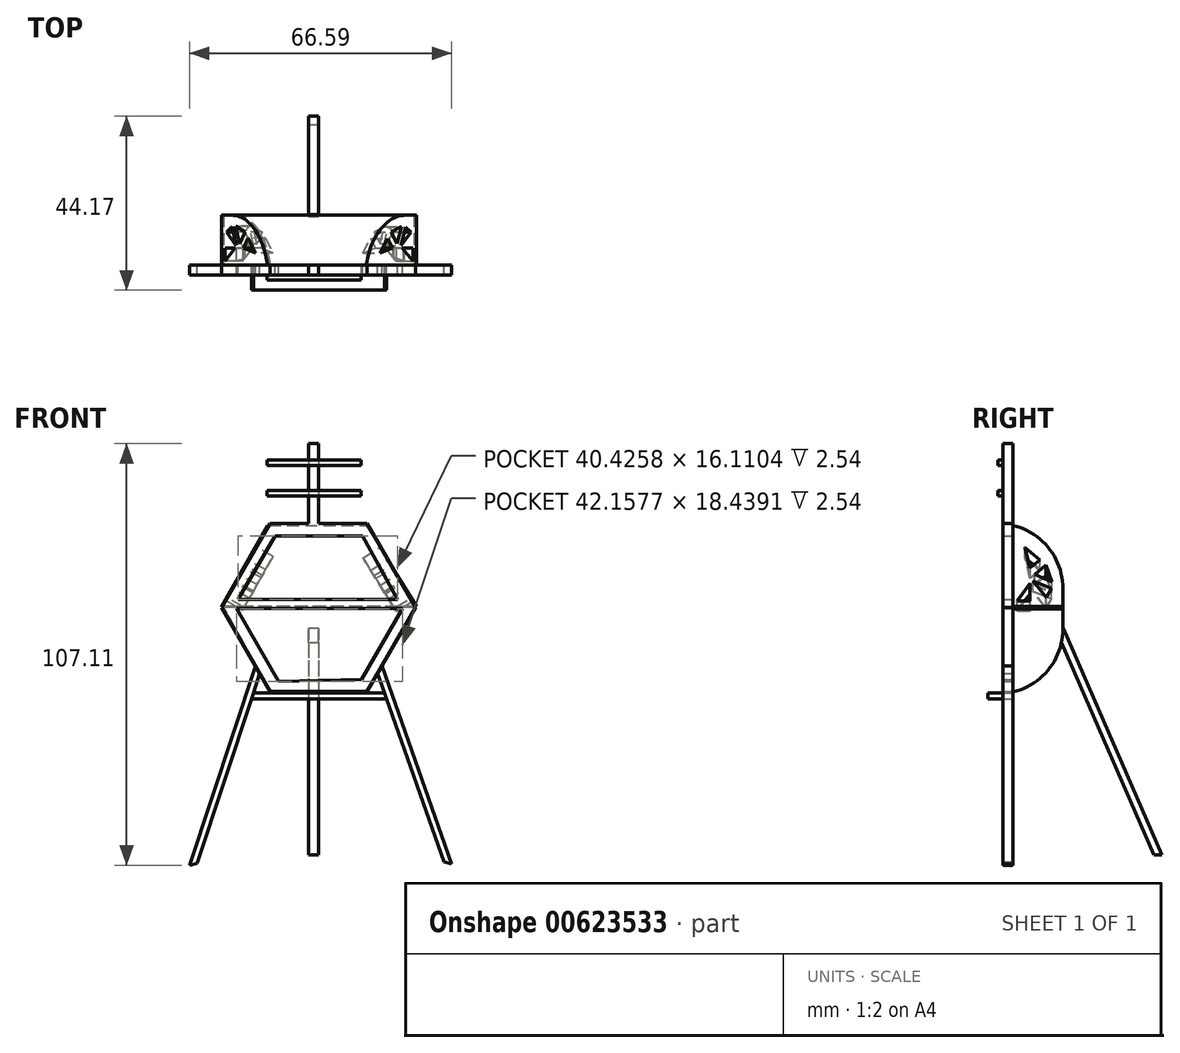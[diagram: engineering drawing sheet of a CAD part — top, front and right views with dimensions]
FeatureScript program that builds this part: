
annotation { "Feature Type Name" : "Feature", "Feature Type Description" : "" }
export const myFeature = defineFeature(function(context is Context, id is Id, definition is map)
    precondition{}
    {
        {
            var Q0;
            Q0=qCreatedBy(makeId("Front.planeOp"),FACE);
            var sketch = newSketch(context, id + "F0", { "sketchPlane" : qUnion([Q0])});
            skCircle(sketch, "E0.cCircle", {"center": v(0, 45.92) * mm, "radius": 21.32 * mm, "construction": true});
            skLineSegment(sketch, "E0.0", {"start": v(12.3, 24.6) * mm, "end": v(-12.3, 24.6) * mm});
            skLineSegment(sketch, "E0.1", {"start": v(-12.3, 24.6) * mm, "end": v(-24.62, 45.92) * mm});
            skLineSegment(sketch, "E0.2", {"start": v(-24.62, 45.92) * mm, "end": v(-12.3, 67.24) * mm});
            skLineSegment(sketch, "E0.3", {"start": v(-12.3, 67.24) * mm, "end": v(12.3, 67.24) * mm});
            skLineSegment(sketch, "E0.4", {"start": v(12.3, 67.24) * mm, "end": v(24.62, 45.92) * mm});
            skLineSegment(sketch, "E0.5", {"start": v(24.62, 45.92) * mm, "end": v(12.3, 24.6) * mm});
            skPoint(sketch, "E0.0.midPoint", {"position": v(0, 24.6) * mm});
            skLineSegment(sketch, "E1", {"start": v(-16.63, 24.26) * mm, "end": v(16.72, 24.26) * mm});
            skLineSegment(sketch, "E2", {"start": v(17.24, 22.76) * mm, "end": v(-17.18, 22.76) * mm});
            skLineSegment(sketch, "E3", {"start": v(-11.12, 64.11) * mm, "end": v(-21.31, 46.45) * mm});
            skLineSegment(sketch, "E4", {"start": v(-21.31, 46.45) * mm, "end": v(-10.18, 27.19) * mm});
            skLineSegment(sketch, "E5", {"start": v(-10.18, 27.19) * mm, "end": v(10.91, 27.6) * mm});
            skLineSegment(sketch, "E6", {"start": v(10.91, 27.6) * mm, "end": v(21.32, 45.62) * mm});
            skLineSegment(sketch, "E7", {"start": v(21.32, 45.62) * mm, "end": v(11.12, 64.11) * mm});
            skLineSegment(sketch, "E8", {"start": v(11.12, 64.11) * mm, "end": v(-11.12, 64.11) * mm});
            skLineSegment(sketch, "E9", {"start": v(-20.42, 48) * mm, "end": v(20, 48) * mm});
            skLineSegment(sketch, "E10", {"start": v(20, 48) * mm, "end": v(21.32, 45.62) * mm});
            skLineSegment(sketch, "E11", {"start": v(21.32, 45.62) * mm, "end": v(-20.84, 45.62) * mm});
            skLineSegment(sketch, "E12", {"start": v(-14.96, 29.2) * mm, "end": v(-30.9, -19.05) * mm});
            skLineSegment(sketch, "E13", {"start": v(14.96, 29.2) * mm, "end": v(31.85, -18.72) * mm});
            skLineSegment(sketch, "E14", {"start": v(-16.06, 31.1) * mm, "end": v(-32.8, -19.55) * mm});
            skLineSegment(sketch, "E15", {"start": v(-32.8, -19.55) * mm, "end": v(-30.9, -19.05) * mm});
            skLineSegment(sketch, "E16", {"start": v(16.07, 31.1) * mm, "end": v(33.8, -19.2) * mm});
            skLineSegment(sketch, "E17", {"start": v(33.8, -19.2) * mm, "end": v(31.85, -18.72) * mm});
            skSolve(sketch);
        }
        {
            var Q0;
            {var subQ4=sQuery(id+"F0.wireOp",EDGE,"E0.0");Q0=makeQuery(id+"F0.imprint","IMPRINT",FACE,{"disambiguationData":[TD([[makeQuery(id+"F0.imprint","IMPRINT",EDGE,{"derivedFrom":subQ4}),-1.0]])]});}
            var Q1;
            {var subQ0=sQuery(id+"F0.wireOp",EDGE,"xqdiFxsL-KJle-jqia-ZrNX-kboYkiIlxZ25");Q1=makeQuery(id+"F0.imprint","IMPRINT",FACE,{"disambiguationData":[TD([[makeQuery(id+"F0.imprint","IMPRINT",EDGE,{"derivedFrom":subQ0}),1.0]])]});}
            var Q2;
            {var subQ0=sQuery(id+"F0.wireOp",EDGE,"LFHcvuUA-xukv-JVWA-ilLV-98vBFIWMlgdJ");Q2=makeQuery(id+"F0.imprint","IMPRINT",FACE,{"disambiguationData":[TD([[makeQuery(id+"F0.imprint","IMPRINT",EDGE,{"derivedFrom":subQ0}),-1.0]])]});}
            extrude(context, id + "F1", {"entities" : qUnion([Q0, Q1, Q2]), "depth" : 2.54 * mm, "offsetDistance" : 25.4 * mm});
        }
        {
            var Q0;
            {var subQ0=sQuery(id+"F0.wireOp",EDGE,"E1");Q0=makeQuery(id+"F0.imprint","IMPRINT",FACE,{"disambiguationData":[TD([[makeQuery(id+"F0.imprint","IMPRINT",EDGE,{"derivedFrom":subQ0}),-1.0]])]});}
            extrude(context, id + "F2", {"entities" : qUnion([Q0]), "operationType" : NewBodyOperationType.ADD, "depth" : 6.35 * mm, "offsetDistance" : 25.4 * mm});
        }
        {
            var Q0;
            {var subQ0=sQuery(id+"F0.wireOp",EDGE,"E9");Q0=makeQuery(id+"F0.imprint","IMPRINT",FACE,{"disambiguationData":[TD([[makeQuery(id+"F0.imprint","IMPRINT",EDGE,{"derivedFrom":subQ0}),-1.0]])]});}
            extrude(context, id + "F3", {"entities" : qUnion([Q0]), "operationType" : NewBodyOperationType.ADD, "depth" : 2.54 * mm, "offsetDistance" : 25.4 * mm});
        }
        {
            var Q0;
            Q0=qCreatedBy(makeId("Front.planeOp"),FACE);
            var sketch = newSketch(context, id + "F4", { "sketchPlane" : qUnion([Q0])});
            skLineSegment(sketch, "E18", {"start": v(24.9, 46.2) * mm, "end": v(-24.6, 46.2) * mm});
            skLineSegment(sketch, "E19", {"start": v(-24.6, 46.2) * mm, "end": v(-13, 66.8) * mm});
            skLineSegment(sketch, "E20", {"start": v(-13, 66.8) * mm, "end": v(12.08, 66.8) * mm});
            skLineSegment(sketch, "E21", {"start": v(12.08, 66.8) * mm, "end": v(24.9, 46.2) * mm});
            skSolve(sketch);
        }
        {
            var Q0;
            Q0 = qSketchRegion(id + "F4", true);
            extrude(context, id + "F5", {"entities" : qUnion([Q0]), "operationType" : NewBodyOperationType.ADD, "oppositeDirection" : true, "depth" : 12.7 * mm, "offsetDistance" : 25.4 * mm});
        }
        {
            var Q0;
            Q0=makeQuery(id+"F5.opExtrude","CAP_EDGE",EDGE,{"disambiguationData":[OSD([sQuery(id+"F4.wireOp",EDGE,"E20")])],"isStart":false});
            fillet(context, id + "F6", {"entities" : qUnion([Q0]), "radius" : 16.5 * mm, "tangentPropagation" : true, "allowEdgeOverflow" : false});
        }
        {
            var Q0;
            {var subQ1=sQuery(id+"F0.wireOp",EDGE,"E0.0");Q0=makeQuery(id+"F0.imprint","IMPRINT",FACE,{"disambiguationData":[TD([[makeQuery(id+"F0.imprint","IMPRINT",EDGE,{"derivedFrom":subQ1}),-1.0]])]});}
            var sketch = newSketch(context, id + "F7", { "sketchPlane" : qUnion([Q0])});
            skLineSegment(sketch, "E22", {"start": v(-24.16, 46.1) * mm, "end": v(24.19, 46.1) * mm});
            skLineSegment(sketch, "E23", {"start": v(24.19, 46.1) * mm, "end": v(24.42, 45.61) * mm});
            skLineSegment(sketch, "E24", {"start": v(24.42, 45.61) * mm, "end": v(12.23, 24.43) * mm});
            skLineSegment(sketch, "E25", {"start": v(12.23, 24.43) * mm, "end": v(-12.24, 24.43) * mm});
            skLineSegment(sketch, "E26", {"start": v(-12.24, 24.43) * mm, "end": v(-24.16, 46.1) * mm});
            skSolve(sketch);
        }
        {
            var Q0;
            Q0 = qSketchRegion(id + "F7", true);
            extrude(context, id + "F8", {"entities" : qUnion([Q0]), "operationType" : NewBodyOperationType.ADD, "oppositeDirection" : true, "depth" : 12.7 * mm, "offsetDistance" : 25.4 * mm});
        }
        {
            var Q0;
            Q0=makeQuery(id+"F8.opExtrude","CAP_EDGE",EDGE,{"disambiguationData":[OSD([sQuery(id+"F7.wireOp",EDGE,"E25")])],"isStart":false});
            fillet(context, id + "F9", {"entities" : qUnion([Q0]), "radius" : 16.5 * mm, "tangentPropagation" : true, "allowEdgeOverflow" : false});
        }
        {
            var Q0;
            Q0=makeQuery(id+"F5.opExtrude","SWEPT_FACE",FACE,{"disambiguationData":[OSD([sQuery(id+"F4.wireOp",EDGE,"E21")])]});
            var sketch = newSketch(context, id + "F10", { "sketchPlane" : qUnion([Q0])});
            skLineSegment(sketch, "E27", {"start": v(3.02, 43.8) * mm, "end": v(6.81, 40.05) * mm});
            skLineSegment(sketch, "E28", {"start": v(6.81, 40.05) * mm, "end": v(4.35, 37.56) * mm});
            skLineSegment(sketch, "E29", {"start": v(4.35, 37.56) * mm, "end": v(3.02, 43.8) * mm});
            skLineSegment(sketch, "E30", {"start": v(8.35, 38.44) * mm, "end": v(5.52, 35.58) * mm});
            skLineSegment(sketch, "E31", {"start": v(5.52, 35.58) * mm, "end": v(9.86, 33.34) * mm});
            skLineSegment(sketch, "E32", {"start": v(9.86, 33.34) * mm, "end": v(8.35, 38.44) * mm});
            skLineSegment(sketch, "E33", {"start": v(5.01, 33.65) * mm, "end": v(9.72, 31.5) * mm});
            skLineSegment(sketch, "E34", {"start": v(9.72, 31.5) * mm, "end": v(8.46, 28.73) * mm});
            skLineSegment(sketch, "E35", {"start": v(8.46, 28.73) * mm, "end": v(5.01, 33.65) * mm});
            skLineSegment(sketch, "E36", {"start": v(4.35, 33) * mm, "end": v(4.35, 27.8) * mm});
            skLineSegment(sketch, "E37", {"start": v(4.35, 27.8) * mm, "end": v(1.1, 27.8) * mm});
            skLineSegment(sketch, "E38", {"start": v(1.1, 27.8) * mm, "end": v(4.35, 33) * mm});
            skSolve(sketch);
        }
        {
            var Q0;
            Q0=makeQuery(id+"F5.opExtrude","SWEPT_FACE",FACE,{"disambiguationData":[OSD([sQuery(id+"F4.wireOp",EDGE,"E19")])]});
            var sketch = newSketch(context, id + "F11", { "sketchPlane" : qUnion([Q0])});
            skLineSegment(sketch, "E39", {"start": v(-3.04, 45.6) * mm, "end": v(-4.37, 39.43) * mm});
            skLineSegment(sketch, "E40", {"start": v(-4.37, 39.43) * mm, "end": v(-6.85, 41.79) * mm});
            skLineSegment(sketch, "E41", {"start": v(-6.85, 41.79) * mm, "end": v(-3.04, 45.6) * mm});
            skLineSegment(sketch, "E42", {"start": v(-8.37, 40.12) * mm, "end": v(-5.4, 37.41) * mm});
            skLineSegment(sketch, "E43", {"start": v(-5.4, 37.41) * mm, "end": v(-9.88, 35.26) * mm});
            skLineSegment(sketch, "E44", {"start": v(-9.88, 35.26) * mm, "end": v(-8.37, 40.12) * mm});
            skLineSegment(sketch, "E45", {"start": v(-9.76, 33.4) * mm, "end": v(-8.37, 30.75) * mm});
            skLineSegment(sketch, "E46", {"start": v(-8.37, 30.75) * mm, "end": v(-5.04, 35.54) * mm});
            skLineSegment(sketch, "E47", {"start": v(-5.04, 35.54) * mm, "end": v(-9.76, 33.4) * mm});
            skLineSegment(sketch, "E48", {"start": v(-4.31, 35.05) * mm, "end": v(-4.31, 29.93) * mm});
            skLineSegment(sketch, "E49", {"start": v(-4.31, 29.93) * mm, "end": v(-1, 29.93) * mm});
            skLineSegment(sketch, "E50", {"start": v(-1, 29.93) * mm, "end": v(-4.31, 35.05) * mm});
            skSolve(sketch);
        }
        {
            var Q0;
            {var subQ6=sQuery(id+"F0.wireOp",EDGE,"E14");Q0=makeQuery(id+"F0.imprint","IMPRINT",FACE,{"disambiguationData":[TD([[makeQuery(id+"F0.imprint","IMPRINT",EDGE,{"derivedFrom":subQ6}),1.0]])]});}
            var Q1;
            {var subQ6=sQuery(id+"F0.wireOp",EDGE,"E16");Q1=makeQuery(id+"F0.imprint","IMPRINT",FACE,{"disambiguationData":[TD([[makeQuery(id+"F0.imprint","IMPRINT",EDGE,{"derivedFrom":subQ6}),-1.0]])]});}
            extrude(context, id + "F12", {"entities" : qUnion([Q0, Q1]), "depth" : 2.54 * mm, "offsetDistance" : 25.4 * mm});
        }
        {
            var Q0;
            Q0=makeQuery(id+"F11.imprint","IMPRINT",FACE,{"disambiguationData":[TD([[makeQuery(id+"F11.imprint","IMPRINT",EDGE,{"derivedFrom":sQuery(id+"F11.wireOp",EDGE,"E39")}),-1.0]])]});
            var Q1;
            Q1=makeQuery(id+"F11.imprint","IMPRINT",FACE,{"disambiguationData":[TD([[makeQuery(id+"F11.imprint","IMPRINT",EDGE,{"derivedFrom":sQuery(id+"F11.wireOp",EDGE,"E42")}),-1.0]])]});
            var Q2;
            Q2=makeQuery(id+"F11.imprint","IMPRINT",FACE,{"disambiguationData":[TD([[makeQuery(id+"F11.imprint","IMPRINT",EDGE,{"derivedFrom":sQuery(id+"F11.wireOp",EDGE,"E45")}),1.0]])]});
            var Q3;
            Q3=makeQuery(id+"F11.imprint","IMPRINT",FACE,{"disambiguationData":[TD([[makeQuery(id+"F11.imprint","IMPRINT",EDGE,{"derivedFrom":sQuery(id+"F11.wireOp",EDGE,"E48")}),1.0]])]});
            var Q4;
            Q4=makeQuery(id+"F10.imprint","IMPRINT",FACE,{"disambiguationData":[TD([[makeQuery(id+"F10.imprint","IMPRINT",EDGE,{"derivedFrom":sQuery(id+"F10.wireOp",EDGE,"E27")}),-1.0]])]});
            var Q5;
            Q5=makeQuery(id+"F10.imprint","IMPRINT",FACE,{"disambiguationData":[TD([[makeQuery(id+"F10.imprint","IMPRINT",EDGE,{"derivedFrom":sQuery(id+"F10.wireOp",EDGE,"E36")}),-1.0]])]});
            var Q6;
            Q6=makeQuery(id+"F10.imprint","IMPRINT",FACE,{"disambiguationData":[TD([[makeQuery(id+"F10.imprint","IMPRINT",EDGE,{"derivedFrom":sQuery(id+"F10.wireOp",EDGE,"E33")}),-1.0]])]});
            var Q7;
            Q7=makeQuery(id+"F10.imprint","IMPRINT",FACE,{"disambiguationData":[TD([[makeQuery(id+"F10.imprint","IMPRINT",EDGE,{"derivedFrom":sQuery(id+"F10.wireOp",EDGE,"E30")}),1.0]])]});
            extrude(context, id + "F13", {"entities" : qUnion([Q0, Q1, Q2, Q3, Q4, Q5, Q6, Q7]), "operationType" : NewBodyOperationType.REMOVE, "oppositeDirection" : true, "depth" : 5.08 * mm, "offsetDistance" : 25.4 * mm});
        }
        {
            var Q0;
            Q0=makeQuery(id+"F10.imprint","IMPRINT",FACE,{"disambiguationData":[TD([[makeQuery(id+"F10.imprint","IMPRINT",EDGE,{"derivedFrom":sQuery(id+"F10.wireOp",EDGE,"E30")}),1.0]])]});
            var Q1;
            Q1=makeQuery(id+"F10.imprint","IMPRINT",FACE,{"disambiguationData":[TD([[makeQuery(id+"F10.imprint","IMPRINT",EDGE,{"derivedFrom":sQuery(id+"F10.wireOp",EDGE,"E33")}),-1.0]])]});
            var Q2;
            Q2=makeQuery(id+"F10.imprint","IMPRINT",FACE,{"disambiguationData":[TD([[makeQuery(id+"F10.imprint","IMPRINT",EDGE,{"derivedFrom":sQuery(id+"F10.wireOp",EDGE,"E36")}),-1.0]])]});
            var Q3;
            Q3=makeQuery(id+"F10.imprint","IMPRINT",FACE,{"disambiguationData":[TD([[makeQuery(id+"F10.imprint","IMPRINT",EDGE,{"derivedFrom":sQuery(id+"F10.wireOp",EDGE,"E27")}),-1.0]])]});
            extrude(context, id + "F14", {"entities" : qUnion([Q0, Q1, Q2, Q3]), "operationType" : NewBodyOperationType.REMOVE, "oppositeDirection" : true, "depth" : 5.08 * mm, "offsetDistance" : 25.4 * mm});
        }
        {
            var Q0;
            Q0=qCreatedBy(makeId("Right.planeOp"),FACE);
            var sketch = newSketch(context, id + "F15", { "sketchPlane" : qUnion([Q0])});
            skLineSegment(sketch, "E51", {"start": v(12.87, 40.67) * mm, "end": v(37.82, -16.89) * mm});
            skLineSegment(sketch, "E52", {"start": v(12.87, 40.67) * mm, "end": v(10.8, 40.67) * mm});
            skLineSegment(sketch, "E53", {"start": v(10.8, 40.67) * mm, "end": v(35.75, -16.89) * mm});
            skLineSegment(sketch, "E54", {"start": v(35.75, -16.89) * mm, "end": v(37.82, -16.89) * mm});
            skSolve(sketch);
        }
        {
            var Q0;
            Q0=makeQuery(id+"F15.imprint","IMPRINT",FACE,{"disambiguationData":[TD([[makeQuery(id+"F15.imprint","IMPRINT",EDGE,{"derivedFrom":sQuery(id+"F15.wireOp",EDGE,"E51")}),-1.0]])]});
            extrude(context, id + "F16", {"entities" : qUnion([Q0]), "operationType" : NewBodyOperationType.ADD, "oppositeDirection" : true, "depth" : 2.54 * mm, "offsetDistance" : 25.4 * mm});
        }
        {
            var Q0;
            Q0=makeQuery(id+"F1.opExtrude","SWEPT_FACE",FACE,{"disambiguationData":[OSD([sQuery(id+"F0.wireOp",EDGE,"E0.3")])]});
            var sketch = newSketch(context, id + "F17", { "sketchPlane" : qUnion([Q0])});
            skLineSegment(sketch, "E55.bottom", {"start": v(-2.55, 0) * mm, "end": v(0, 0) * mm});
            skLineSegment(sketch, "E55.top", {"start": v(-2.55, -2.54) * mm, "end": v(0, -2.54) * mm});
            skLineSegment(sketch, "E55.left", {"start": v(-2.55, 0) * mm, "end": v(-2.55, -2.54) * mm});
            skLineSegment(sketch, "E55.right", {"start": v(0, 0) * mm, "end": v(0, -2.54) * mm});
            skSolve(sketch);
        }
        {
            var Q0;
            Q0=makeQuery(id+"F17.imprint","IMPRINT",FACE,{"disambiguationData":[TD([[makeQuery(id+"F17.imprint","IMPRINT",EDGE,{"derivedFrom":sQuery(id+"F17.wireOp",EDGE,"E55.bottom")}),-1.0]])]});
            extrude(context, id + "F18", {"entities" : qUnion([Q0]), "operationType" : NewBodyOperationType.ADD, "depth" : 20.32 * mm, "offsetDistance" : 25.4 * mm});
        }
        {
            var Q0;
            {var subQ0=sQuery(id+"F0.wireOp",EDGE,"E10");var subQ1=sQuery(id+"F0.wireOp",EDGE,"E4");var subQ2=sQuery(id+"F0.wireOp",EDGE,"E3");Q0=makeQuery(id+"F18.boolean.opBoolean","MERGE",FACE,{"derivedFrom":[makeQuery(id+"F3.boolean.opBoolean","MERGE",FACE,{"derivedFrom":[makeQuery(id+"F1.opExtrude","CAP_FACE",FACE,{"disambiguationData":[OSD([sQuery(id+"F0.wireOp",EDGE,"E0.0"),sQuery(id+"F0.wireOp",EDGE,"E0.1"),sQuery(id+"F0.wireOp",EDGE,"E0.2"),sQuery(id+"F0.wireOp",EDGE,"E0.3"),sQuery(id+"F0.wireOp",EDGE,"E0.4"),sQuery(id+"F0.wireOp",EDGE,"E0.5"),subQ2,subQ1,sQuery(id+"F0.wireOp",EDGE,"E5"),sQuery(id+"F0.wireOp",EDGE,"E6"),sQuery(id+"F0.wireOp",EDGE,"E7"),sQuery(id+"F0.wireOp",EDGE,"E8"),subQ0])],"isStart":false}),makeQuery(id+"F3.opExtrude","CAP_FACE",FACE,{"disambiguationData":[OSD([subQ2,subQ1,sQuery(id+"F0.wireOp",EDGE,"E9"),subQ0,sQuery(id+"F0.wireOp",EDGE,"E11")])],"isStart":false})]}),makeQuery(id+"F18.opExtrude","SWEPT_FACE",FACE,{"disambiguationData":[OSD([sQuery(id+"F17.wireOp",EDGE,"E55.top")])]})]});}
            var sketch = newSketch(context, id + "F19", { "sketchPlane" : qUnion([Q0])});
            skLineSegment(sketch, "E56.bottom", {"start": v(-13.07, 83.42) * mm, "end": v(10.76, 83.42) * mm});
            skLineSegment(sketch, "E56.top", {"start": v(-13.07, 82.02) * mm, "end": v(10.76, 82.02) * mm});
            skLineSegment(sketch, "E56.left", {"start": v(-13.07, 83.42) * mm, "end": v(-13.07, 82.02) * mm});
            skLineSegment(sketch, "E56.right", {"start": v(10.76, 83.42) * mm, "end": v(10.76, 82.02) * mm});
            skLineSegment(sketch, "E57.bottom", {"start": v(-13.07, 75.67) * mm, "end": v(10.76, 75.67) * mm});
            skLineSegment(sketch, "E57.top", {"start": v(-13.07, 74.27) * mm, "end": v(10.76, 74.27) * mm});
            skLineSegment(sketch, "E57.left", {"start": v(-13.07, 75.67) * mm, "end": v(-13.07, 74.27) * mm});
            skLineSegment(sketch, "E57.right", {"start": v(10.76, 75.67) * mm, "end": v(10.76, 74.27) * mm});
            skSolve(sketch);
        }
        {
            var Q0;
            {var subQ0=sQuery(id+"F19.wireOp",EDGE,"E56.left");Q0=makeQuery(id+"F19.imprint","IMPRINT",FACE,{"disambiguationData":[TD([[makeQuery(id+"F19.imprint","IMPRINT",EDGE,{"derivedFrom":subQ0}),1.0]])]});}
            var Q1;
            {var subQ0=sQuery(id+"F19.wireOp",EDGE,"E56.right");Q1=makeQuery(id+"F19.imprint","IMPRINT",FACE,{"disambiguationData":[TD([[makeQuery(id+"F19.imprint","IMPRINT",EDGE,{"derivedFrom":subQ0}),-1.0]])]});}
            var Q2;
            {var subQ0=sQuery(id+"F19.wireOp",EDGE,"E56.bottom");var subQ1=sQuery(id+"F17.wireOp",EDGE,"E55.top");var subQ2=sQuery(id+"F0.wireOp",EDGE,"E0.3");var subQ3=makeQuery(id+"F18.opExtrude","SWEPT_EDGE",EDGE,{"disambiguationData":[OSD([subQ2,subQ1,sQuery(id+"F17.wireOp",EDGE,"E55.left")])]});var subQ4=makeQuery(id+"F19.imprint","INTERSECT",VERTEX,{"derivedFrom":[subQ3,subQ0]});Q2=makeQuery(id+"F19.imprint","IMPRINT",FACE,{"disambiguationData":[TD([[makeQuery(id+"F19.imprint","IMPRINT",EDGE,{"disambiguationData":[TD([[subQ4,-1.0]])],"derivedFrom":subQ0}),-1.0]])]});}
            var Q3;
            {var subQ0=sQuery(id+"F19.wireOp",EDGE,"E57.left");Q3=makeQuery(id+"F19.imprint","IMPRINT",FACE,{"disambiguationData":[TD([[makeQuery(id+"F19.imprint","IMPRINT",EDGE,{"derivedFrom":subQ0}),1.0]])]});}
            var Q4;
            {var subQ0=sQuery(id+"F19.wireOp",EDGE,"E57.bottom");var subQ1=sQuery(id+"F17.wireOp",EDGE,"E55.top");var subQ2=sQuery(id+"F0.wireOp",EDGE,"E0.3");var subQ3=makeQuery(id+"F18.opExtrude","SWEPT_EDGE",EDGE,{"disambiguationData":[OSD([subQ2,subQ1,sQuery(id+"F17.wireOp",EDGE,"E55.left")])]});var subQ4=makeQuery(id+"F19.imprint","INTERSECT",VERTEX,{"derivedFrom":[subQ3,subQ0]});Q4=makeQuery(id+"F19.imprint","IMPRINT",FACE,{"disambiguationData":[TD([[makeQuery(id+"F19.imprint","IMPRINT",EDGE,{"disambiguationData":[TD([[subQ4,-1.0]])],"derivedFrom":subQ0}),-1.0]])]});}
            var Q5;
            {var subQ0=sQuery(id+"F19.wireOp",EDGE,"E57.right");Q5=makeQuery(id+"F19.imprint","IMPRINT",FACE,{"disambiguationData":[TD([[makeQuery(id+"F19.imprint","IMPRINT",EDGE,{"derivedFrom":subQ0}),-1.0]])]});}
            extrude(context, id + "F20", {"entities" : qUnion([Q0, Q1, Q2, Q3, Q4, Q5]), "operationType" : NewBodyOperationType.ADD, "depth" : 1.27 * mm, "offsetDistance" : 25.4 * mm});
        }
    });
